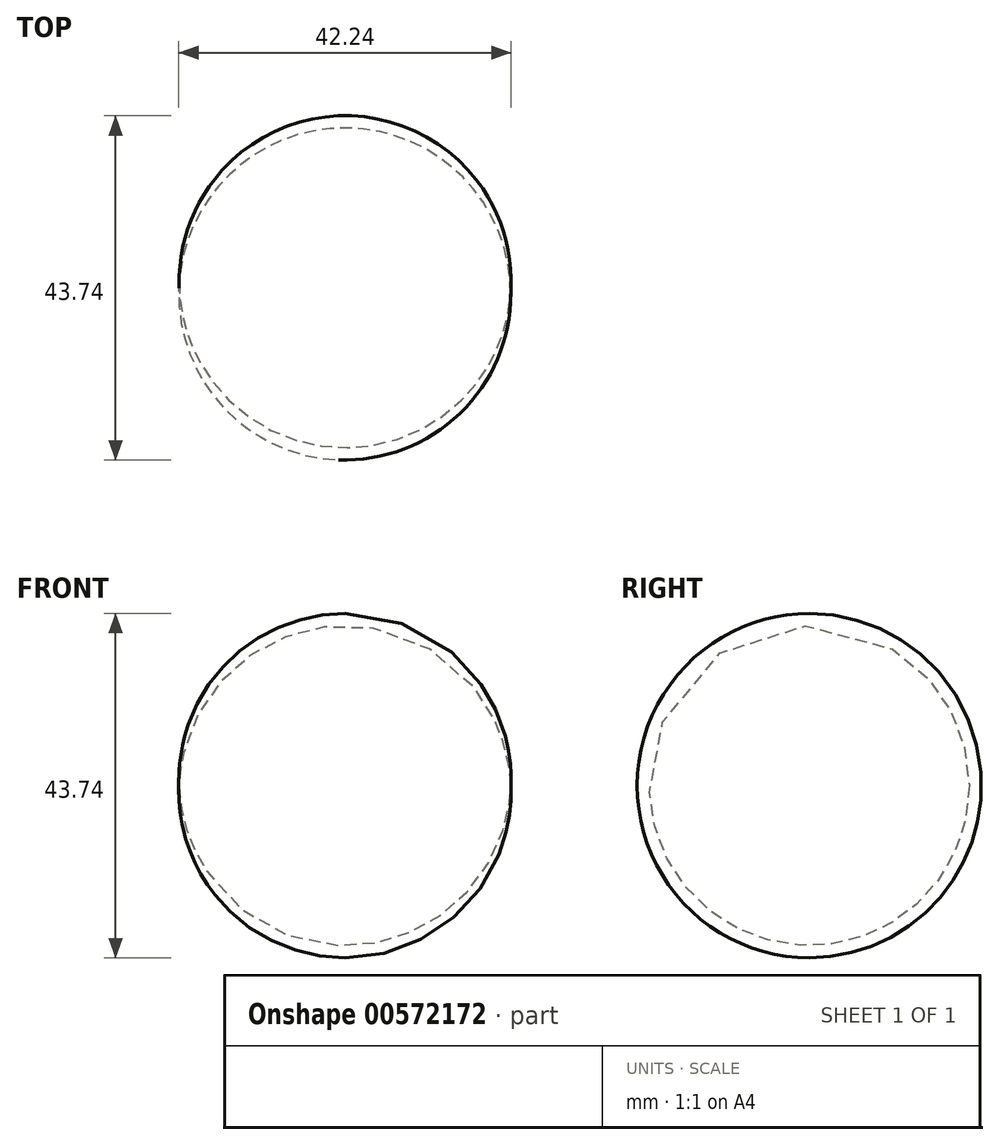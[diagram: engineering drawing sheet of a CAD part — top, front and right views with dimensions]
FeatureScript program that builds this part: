
annotation { "Feature Type Name" : "Feature", "Feature Type Description" : "" }
export const myFeature = defineFeature(function(context is Context, id is Id, definition is map)
    precondition{}
    {
        {
            var Q0;
            Q0=qCreatedBy(makeId("Top.planeOp"),FACE);
            var sketch = newSketch(context, id + "F0", { "sketchPlane" : qUnion([Q0])});
            skCircle(sketch, "E0", {"center": v(0, 0) * mm, "radius": 21.09 * mm});
            skLineSegment(sketch, "E1", {"start": v(-21.09, 0) * mm, "end": v(21.03, -1.56) * mm});
            skSolve(sketch);
        }
        {
            var Q0;
            {var subQ0=sQuery(id+"F0.wireOp",EDGE,"E1");Q0=makeQuery(id+"F0.imprint","IMPRINT",FACE,{"disambiguationData":[TD([[makeQuery(id+"F0.imprint","IMPRINT",EDGE,{"derivedFrom":subQ0}),1.0]])]});}
            var Q1;
            Q1=sQuery(id+"F0.wireOp",EDGE,"E1");
            revolve(context, id + "F1", {"entities" : qUnion([Q0]), "axis" : qUnion([Q1]), "revolveType" : RevolveType.FULL});
        }
    });
